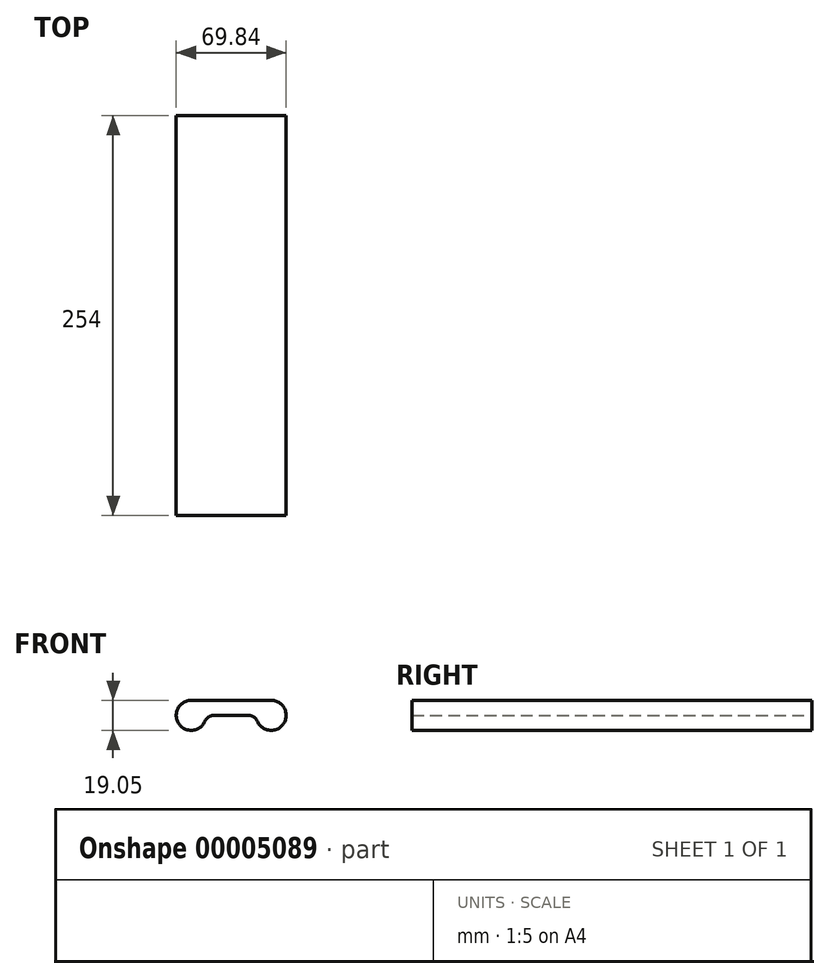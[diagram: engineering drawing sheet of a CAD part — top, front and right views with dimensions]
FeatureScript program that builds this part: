
annotation { "Feature Type Name" : "Feature", "Feature Type Description" : "" }
export const myFeature = defineFeature(function(context is Context, id is Id, definition is map)
    precondition{}
    {
        {
            var Q0;
            Q0=qCreatedBy(makeId("Front.planeOp"),FACE);
            var sketch = newSketch(context, id + "F0", { "sketchPlane" : qUnion([Q0])});
            skLineSegment(sketch, "E0", {"start": v(-25.4, 0) * mm, "end": v(25.4, 0) * mm});
            skArc(sketch, "E1", {"start": v(25.4, 0) * mm, "mid": v(33.37, -14.74) * mm, "end": v(16.67, -13.33) * mm});
            skLineSegment(sketch, "E2", {"start": v(10.85, -9.53) * mm, "end": v(0, -9.53) * mm});
            skLineSegment(sketch, "E3.0.MirrorCS", {"start": v(-10.85, -9.53) * mm, "end": v(0, -9.53) * mm});
            skArc(sketch, "E4.0.MirrorCS", {"start": v(-25.4, 0) * mm, "mid": v(-33.37, -14.74) * mm, "end": v(-16.67, -13.33) * mm});
            skLineSegment(sketch, "E5.0.MirrorCS", {"start": v(15.88, -9.52) * mm, "end": v(0, -9.53) * mm});
            skLineSegment(sketch, "E6.0.MirrorCS", {"start": v(25.4, 0) * mm, "end": v(-25.4, 0) * mm});
            skPoint(sketch, "E7.visualSharp", {"position": v(-15.88, -9.53) * mm});
            skArc(sketch, "E7.filletArc", {"start": v(-10.85, -9.53) * mm, "mid": v(-14.33, -10.56) * mm, "end": v(-16.67, -13.33) * mm});
            skPoint(sketch, "E8.visualSharp", {"position": v(15.88, -9.52) * mm});
            skArc(sketch, "E8.filletArc", {"start": v(16.67, -13.33) * mm, "mid": v(14.33, -10.56) * mm, "end": v(10.85, -9.53) * mm});
            skSolve(sketch);
        }
        {
            var Q0;
            Q0 = qSketchRegion(id + "F0", true);
            extrude(context, id + "F1", {"entities" : qUnion([Q0]), "endBound" : BoundingType.SYMMETRIC, "depth" : 254 * mm});
        }
    });
